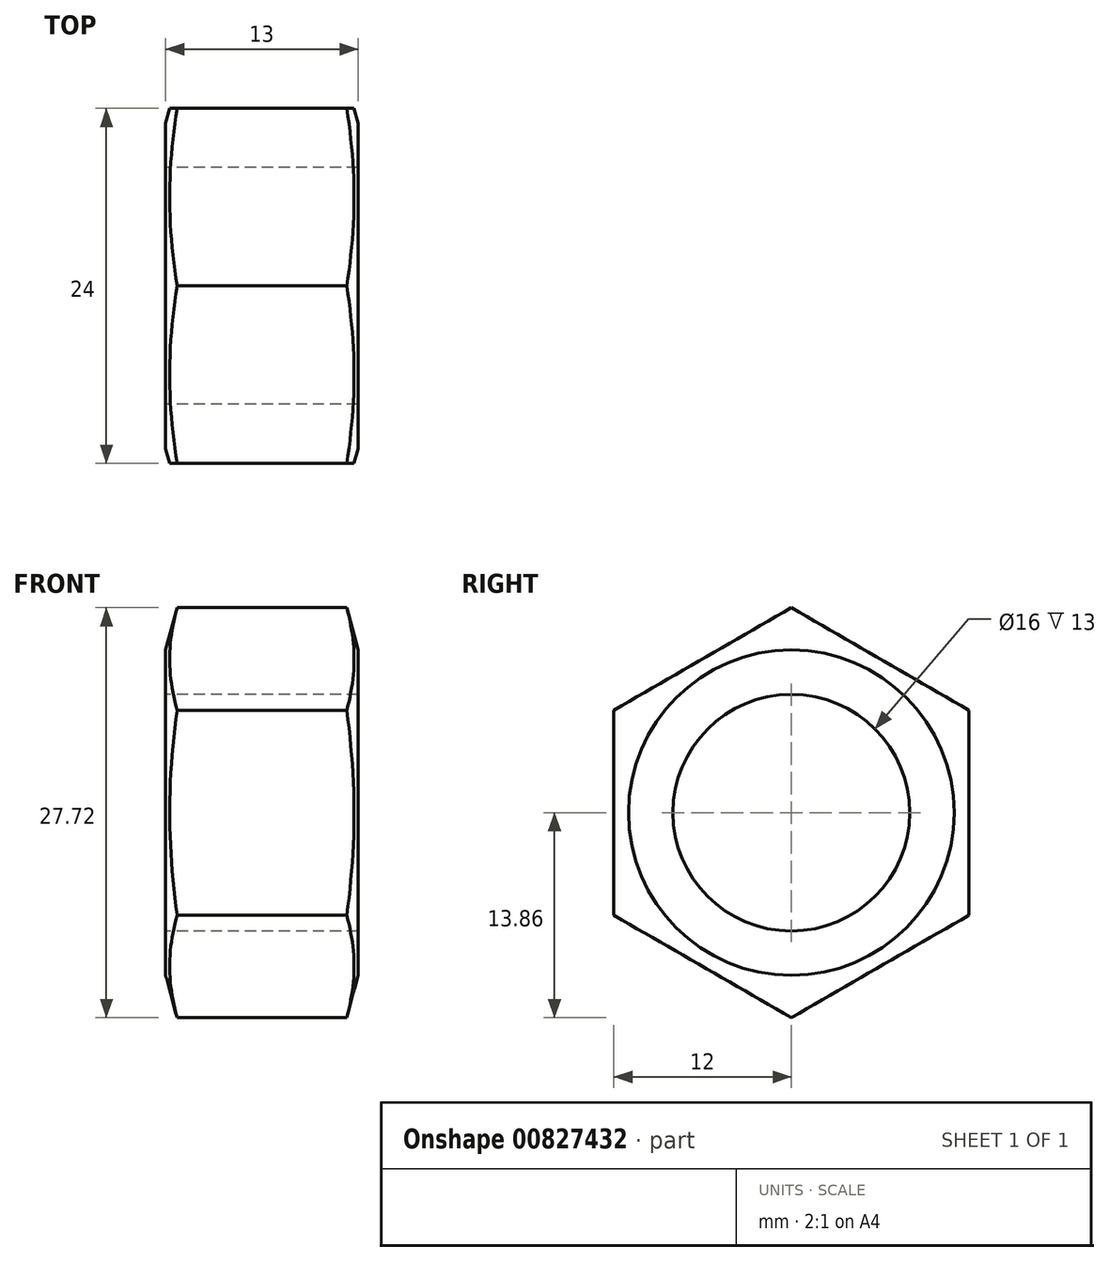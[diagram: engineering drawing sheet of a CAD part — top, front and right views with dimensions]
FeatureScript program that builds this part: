
annotation { "Feature Type Name" : "Feature", "Feature Type Description" : "" }
export const myFeature = defineFeature(function(context is Context, id is Id, definition is map)
    precondition{}
    {
        {
            var Q0;
            Q0=qCreatedBy(makeId("Right.planeOp"),FACE);
            var sketch = newSketch(context, id + "F0", { "sketchPlane" : qUnion([Q0])});
            skCircle(sketch, "E0.cCircle", {"center": v(0, 0) * mm, "radius": 13.86 * mm, "construction": true});
            skLineSegment(sketch, "E0.0", {"start": v(0, 13.86) * mm, "end": v(12, 6.93) * mm});
            skLineSegment(sketch, "E0.1", {"start": v(12, 6.93) * mm, "end": v(12, -6.93) * mm});
            skLineSegment(sketch, "E0.2", {"start": v(12, -6.93) * mm, "end": v(0, -13.86) * mm});
            skLineSegment(sketch, "E0.3", {"start": v(0, -13.86) * mm, "end": v(-12, -6.93) * mm});
            skLineSegment(sketch, "E0.4", {"start": v(-12, -6.93) * mm, "end": v(-12, 6.93) * mm});
            skLineSegment(sketch, "E0.5", {"start": v(-12, 6.93) * mm, "end": v(0, 13.86) * mm});
            skCircle(sketch, "E1", {"center": v(0, 0) * mm, "radius": 8 * mm});
            skSolve(sketch);
        }
        {
            var Q0;
            Q0=makeQuery(id+"F0.imprint","IMPRINT",FACE,{"disambiguationData":[TD([[makeQuery(id+"F0.imprint","IMPRINT",EDGE,{"derivedFrom":sQuery(id+"F0.wireOp",EDGE,"E0.0")}),-1.0]])]});
            extrude(context, id + "F1", {"entities" : qUnion([Q0]), "depth" : 13 * mm, "offsetDistance" : 25 * mm});
        }
        {
            var Q0;
            Q0=qCreatedBy(makeId("Front.planeOp"),FACE);
            var sketch = newSketch(context, id + "F2", { "sketchPlane" : qUnion([Q0])});
            skLineSegment(sketch, "E2", {"start": v(0, 11) * mm, "end": v(3.63, 24.53) * mm});
            skLineSegment(sketch, "E3", {"start": v(3.63, 24.53) * mm, "end": v(0, 24.53) * mm});
            skLineSegment(sketch, "E4", {"start": v(0, 24.53) * mm, "end": v(0, 11) * mm});
            skLineSegment(sketch, "E5", {"start": v(6.5, 27.91) * mm, "end": v(6.5, -18.43) * mm, "construction": true});
            skLineSegment(sketch, "E6.MirrorCS", {"start": v(13, 11) * mm, "end": v(9.37, 24.53) * mm});
            skLineSegment(sketch, "E7.MirrorCS", {"start": v(9.37, 24.53) * mm, "end": v(13, 24.53) * mm});
            skLineSegment(sketch, "E8.MirrorCS", {"start": v(13, 24.53) * mm, "end": v(13, 11) * mm});
            skLineSegment(sketch, "E9", {"start": v(0, 0) * mm, "end": v(80.74, 0) * mm, "construction": true});
            skSolve(sketch);
        }
        {
            var Q0;
            Q0=makeQuery(id+"F2.imprint","IMPRINT",FACE,{"disambiguationData":[TD([[makeQuery(id+"F2.imprint","IMPRINT",EDGE,{"derivedFrom":sQuery(id+"F2.wireOp",EDGE,"E2")}),1.0]])]});
            var Q1;
            Q1=makeQuery(id+"F2.imprint","IMPRINT",FACE,{"disambiguationData":[TD([[makeQuery(id+"F2.imprint","IMPRINT",EDGE,{"derivedFrom":sQuery(id+"F2.wireOp",EDGE,"E6.MirrorCS")}),-1.0]])]});
            var Q2;
            Q2=sQuery(id+"F2.wireOp",EDGE,"E9");
            revolve(context, id + "F3", {"operationType" : NewBodyOperationType.REMOVE, "surfaceOperationType" : NewSurfaceOperationType.NEW, "entities" : qUnion([Q0, Q1]), "axis" : qUnion([Q2]), "revolveType" : RevolveType.FULL, "oppositeDirection" : true});
        }
    });
